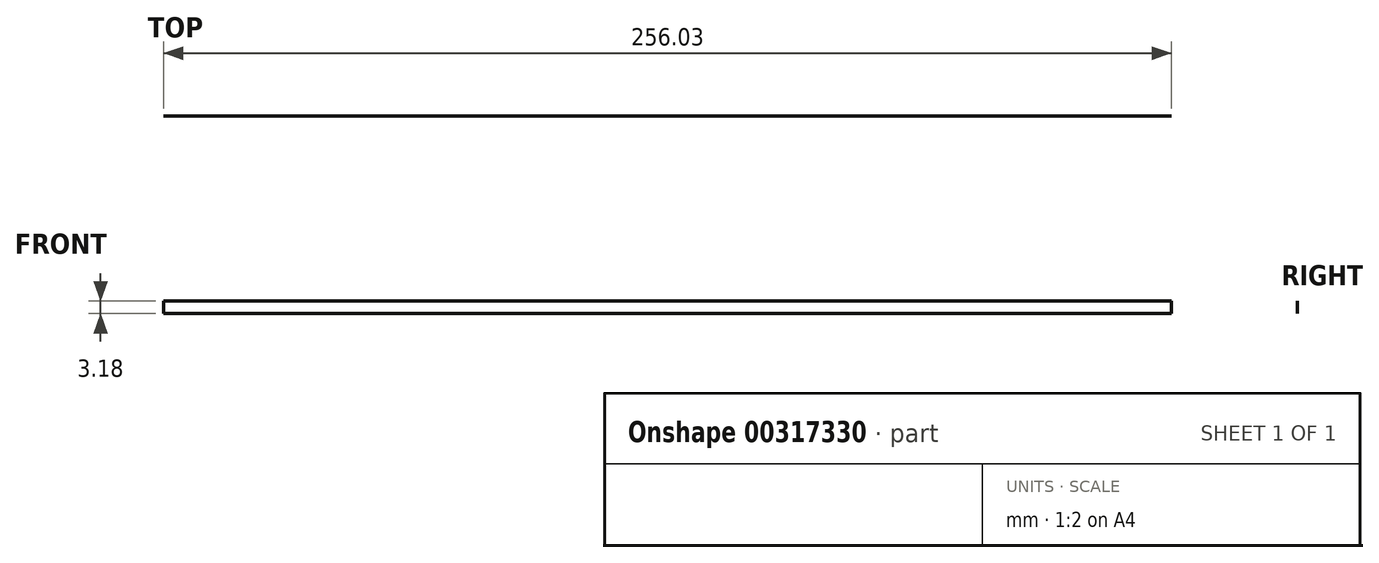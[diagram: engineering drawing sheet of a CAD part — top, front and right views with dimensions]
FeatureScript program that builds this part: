
annotation { "Feature Type Name" : "Feature", "Feature Type Description" : "" }
export const myFeature = defineFeature(function(context is Context, id is Id, definition is map)
    precondition{}
    {
        {
            var Q0;
            Q0=qCreatedBy(makeId("Front.planeOp"),FACE);
            var sketch = newSketch(context, id + "F0", { "sketchPlane" : qUnion([Q0])});
            skLineSegment(sketch, "E0.bottom", {"start": v(-105.05, -7.02) * mm, "end": v(150.98, -7.02) * mm});
            skLineSegment(sketch, "E0.top", {"start": v(-105.05, -10.2) * mm, "end": v(150.98, -10.2) * mm});
            skLineSegment(sketch, "E0.left", {"start": v(-105.05, -7.02) * mm, "end": v(-105.05, -10.2) * mm});
            skLineSegment(sketch, "E0.right", {"start": v(150.98, -7.02) * mm, "end": v(150.98, -10.2) * mm});
            skPoint(sketch, "E0.middle", {"position": v(22.96, -8.6) * mm});
            skSolve(sketch);
        }
        {
            var Q0;
            Q0=qSketchRegion(id+"F0",true);
            extrude(context, id + "F1", {"entities" : qUnion([Q0]), "depth" : 1 / 203.2 * mm});
        }
    });
